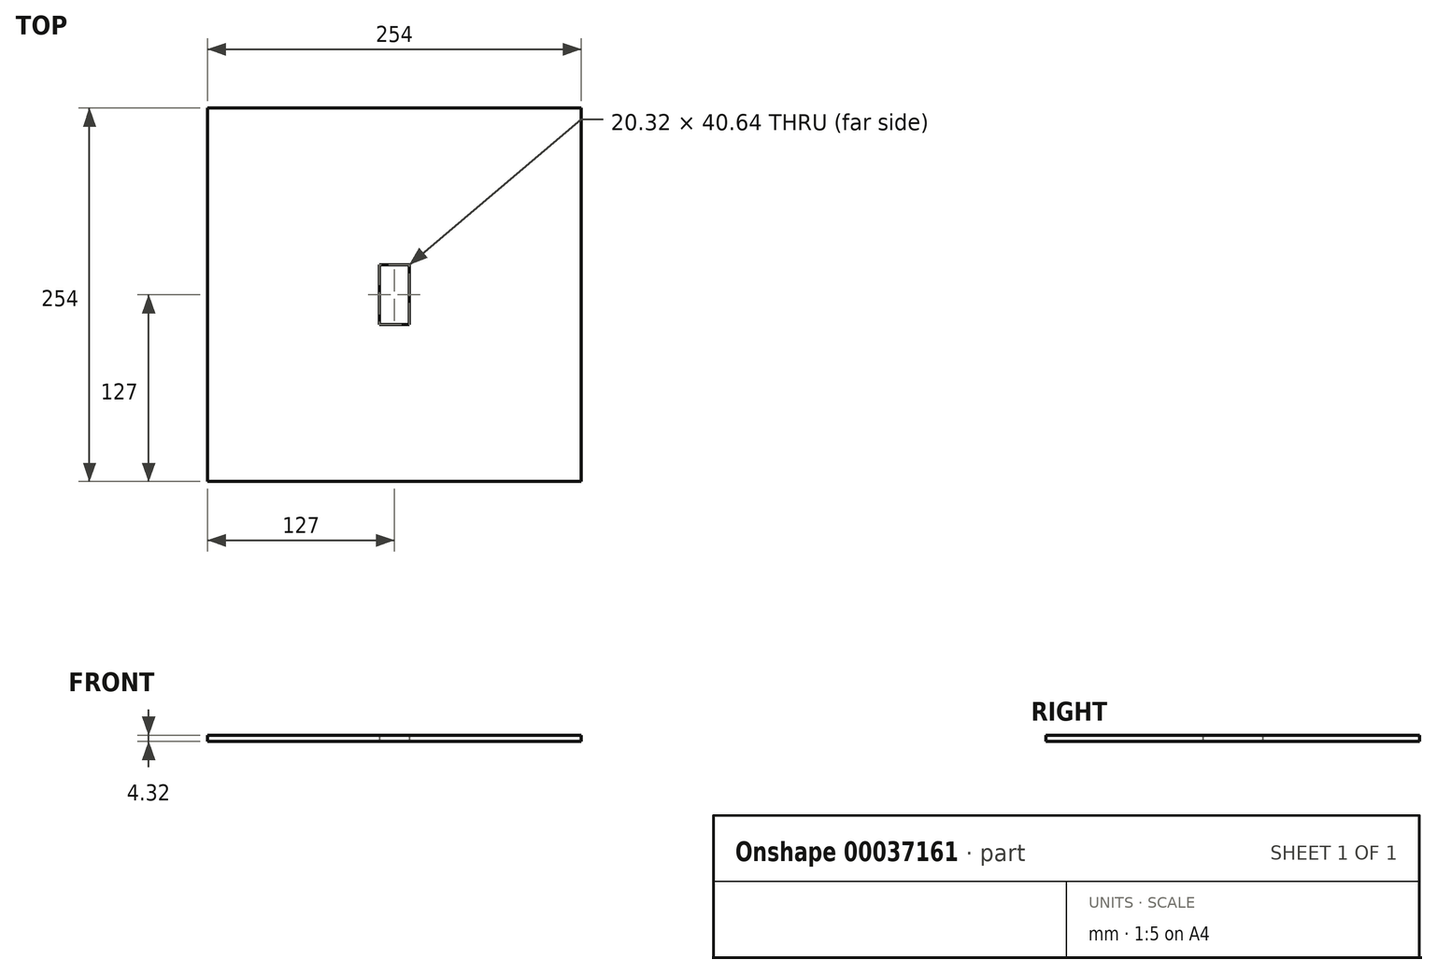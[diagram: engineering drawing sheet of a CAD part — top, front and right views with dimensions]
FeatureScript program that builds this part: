
annotation { "Feature Type Name" : "Feature", "Feature Type Description" : "" }
export const myFeature = defineFeature(function(context is Context, id is Id, definition is map)
    precondition{}
    {
        {
            var Q0;
            Q0=qCreatedBy(makeId("Top.planeOp"),FACE);
            var sketch = newSketch(context, id + "F0", { "sketchPlane" : qUnion([Q0])});
            skLineSegment(sketch, "E0.rect.bottom", {"start": v(-127, 127) * mm, "end": v(127, 127) * mm});
            skLineSegment(sketch, "E0.rect.top", {"start": v(-127, -127) * mm, "end": v(127, -127) * mm});
            skLineSegment(sketch, "E0.rect.left", {"start": v(-127, 127) * mm, "end": v(-127, -127) * mm});
            skLineSegment(sketch, "E0.rect.right", {"start": v(127, 127) * mm, "end": v(127, -127) * mm});
            skPoint(sketch, "E0.rect.middle", {"position": v(0, 0) * mm});
            skLineSegment(sketch, "E1.rect.bottom", {"start": v(-10.16, 20.32) * mm, "end": v(10.16, 20.32) * mm});
            skLineSegment(sketch, "E1.rect.top", {"start": v(-10.16, -20.32) * mm, "end": v(10.16, -20.32) * mm});
            skLineSegment(sketch, "E1.rect.left", {"start": v(-10.16, 20.32) * mm, "end": v(-10.16, -20.32) * mm});
            skLineSegment(sketch, "E1.rect.right", {"start": v(10.16, 20.32) * mm, "end": v(10.16, -20.32) * mm});
            skSolve(sketch);
        }
        {
            var Q0;
            Q0=makeQuery(id+"F0.imprint","IMPRINT",FACE,{"disambiguationData":[TD([[makeQuery(id+"F0.imprint","IMPRINT",EDGE,{"derivedFrom":sQuery(id+"F0.wireOp",EDGE,"E0.rect.bottom")}),-1.0]])]});
            extrude(context, id + "F1", {"entities" : qUnion([Q0]), "depth" : 4.32 * mm});
        }
    });
